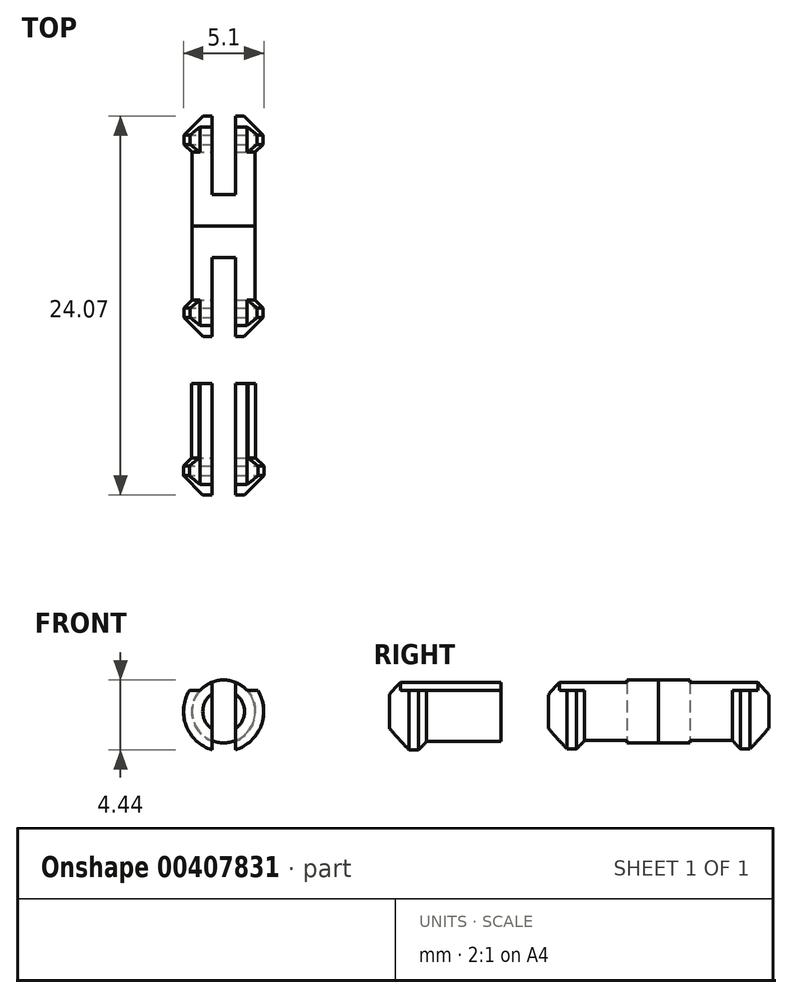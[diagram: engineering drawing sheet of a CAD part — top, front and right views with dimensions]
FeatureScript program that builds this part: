
annotation { "Feature Type Name" : "Feature", "Feature Type Description" : "" }
export const myFeature = defineFeature(function(context is Context, id is Id, definition is map)
    precondition{}
    {
        {
            var Q0;
            Q0=qCreatedBy(makeId("Front.planeOp"),FACE);
            var sketch = newSketch(context, id + "F0", { "sketchPlane" : qUnion([Q0])});
            skCircle(sketch, "E0", {"center": v(0, 0) * mm, "radius": 2 * mm});
            skLineSegment(sketch, "E1", {"start": v(-2, 0) * mm, "end": v(2, 0) * mm, "construction": true});
            skSolve(sketch);
        }
        {
            var Q0;
            Q0=makeQuery(id+"F0.imprint","IMPRINT",FACE,{"disambiguationData":[TD([[makeQuery(id+"F0.imprint","IMPRINT",EDGE,{"derivedFrom":sQuery(id+"F0.wireOp",EDGE,"E0")}),1.0]])]});
            extrude(context, id + "F1", {"entities" : qUnion([Q0]), "depth" : 4 * mm});
        }
        {
            var Q0;
            Q0=makeQuery(id+"F1.opExtrude","CAP_FACE",FACE,{"disambiguationData":[OSD([sQuery(id+"F0.wireOp",EDGE,"E0")])],"isStart":false});
            var sketch = newSketch(context, id + "F2", { "sketchPlane" : qUnion([Q0])});
            skCircle(sketch, "E2.0", {"center": v(0, 0) * mm, "radius": 2.5 * mm});
            skSolve(sketch);
        }
        {
            var Q0;
            Q0=makeQuery(id+"F2.imprint","IMPRINT",FACE,{"disambiguationData":[TD([[makeQuery(id+"F2.imprint","IMPRINT",EDGE,{"derivedFrom":makeQuery(id+"F1.opExtrude","CAP_EDGE",EDGE,{"disambiguationData":[OSD([sQuery(id+"F0.wireOp",EDGE,"E0")])],"isStart":false})}),1.0]])]});
            var Q1;
            Q1=makeQuery(id+"F2.imprint","IMPRINT",FACE,{"disambiguationData":[TD([[makeQuery(id+"F2.imprint","IMPRINT",EDGE,{"derivedFrom":sQuery(id+"F2.wireOp",EDGE,"E2.0")}),1.0]])]});
            var Q2;
            Q2=sQuery(id+"F2.wireOp",EDGE,"E2.0");
            extrude(context, id + "F3", {"entities" : qUnion([Q0, Q1]), "operationType" : NewBodyOperationType.ADD, "surfaceEntities" : qUnion([Q2]), "depth" : 3 * mm});
        }
        {
            var Q0;
            Q0=makeQuery(id+"F3.opExtrude","CAP_EDGE",EDGE,{"disambiguationData":[OSD([sQuery(id+"F2.wireOp",EDGE,"E2.0")])],"isStart":false});
            var Q1;
            Q1=makeQuery(id+"F3.opExtrude","CAP_EDGE",EDGE,{"disambiguationData":[OSD([sQuery(id+"F2.wireOp",EDGE,"E2.0")])],"isStart":true});
            chamfer(context, id + "F4", {"entities" : qUnion([Q0, Q1]), "chamferType" : ChamferType.OFFSET_ANGLE, "width" : 1.2 * mm, "oppositeDirection" : false, "angle" : 45 * degree, "tangentPropagation" : true});
        }
        {
            var Q0;
            Q0=qCreatedBy(makeId("Right.planeOp"),FACE);
            var sketch = newSketch(context, id + "F5", { "sketchPlane" : qUnion([Q0])});
            skLineSegment(sketch, "E3.0", {"start": v(-7, -1.3) * mm, "end": v(-7, 1.3) * mm, "construction": true});
            skLineSegment(sketch, "E4.0", {"start": v(0, -2) * mm, "end": v(0, 2) * mm, "construction": true});
            skLineSegment(sketch, "E5", {"start": v(0, 0) * mm, "end": v(-7, 0) * mm, "construction": true});
            skPoint(sketch, "E6", {"position": v(-3.5, 0) * mm});
            skSolve(sketch);
        }
        {
            var Q0;
            Q0=makeQuery(id+"F1.opExtrude","SWEPT_BODY",BODY,{"disambiguationData":[OSD([sQuery(id+"F0.wireOp",EDGE,"E0")])]});
            var Q1;
            Q1=sQuery(id+"F5.wireOp",VERTEX,"E6");
            transform(context, id + "F6", {"entities" : qUnion([Q0]), "transformType" : TransformType.SCALE_UNIFORMLY, "scale" : 1.02, "scalePoint" : qUnion([Q1]), "makeCopy" : true});
        }
        {
            var Q0;
            Q0=makeQuery(id+"F6.opPattern","COPY",FACE,{"derivedFrom":makeQuery(id+"F1.opExtrude","CAP_FACE",FACE,{"disambiguationData":[OSD([sQuery(id+"F0.wireOp",EDGE,"E0")])],"isStart":true}),"instanceName":"1"});
            var Q1;
            Q1=makeQuery(id+"F1.opExtrude","CAP_FACE",FACE,{"disambiguationData":[OSD([sQuery(id+"F0.wireOp",EDGE,"E0")])],"isStart":true});
            extrude(context, id + "F7", {"entities" : qUnion([Q0]), "operationType" : NewBodyOperationType.REMOVE, "endBound" : BoundingType.UP_TO_SURFACE, "oppositeDirection" : true, "endBoundEntityFace" : qUnion([Q1]), "depth" : 25 * mm});
        }
        {
            var Q0;
            Q0=makeQuery(id+"F6.opPattern","COPY",BODY,{"derivedFrom":makeQuery(id+"F1.opExtrude","SWEPT_BODY",BODY,{"disambiguationData":[OSD([sQuery(id+"F0.wireOp",EDGE,"E0")])]}),"instanceName":"1"});
            var Q1;
            Q1=sQuery(id+"F5.wireOp",EDGE,"E5");
            transform(context, id + "F8", {"entities" : qUnion([Q0]), "transformType" : TransformType.TRANSLATION_DISTANCE, "transformDirection" : qUnion([Q1]), "distance" : 10 * mm, "makeCopy" : false});
        }
        {
            var Q0;
            Q0=qCreatedBy(makeId("Right.planeOp"),FACE);
            var sketch = newSketch(context, id + "F9", { "sketchPlane" : qUnion([Q0])});
            skPoint(sketch, "E7.0", {"position": v(0, 0) * mm});
            skLineSegment(sketch, "E8", {"start": v(0, 0) * mm, "end": v(-2, 0) * mm, "construction": true});
            skSolve(sketch);
        }
        {
            var Q0;
            Q0=makeQuery(id+"F0.imprint","IMPRINT",FACE,{"disambiguationData":[TD([[makeQuery(id+"F0.imprint","IMPRINT",EDGE,{"derivedFrom":sQuery(id+"F0.wireOp",EDGE,"E0")}),1.0]])]});
            var Q1;
            Q1=sQuery(id+"F9.wireOp",VERTEX,"E8.end");
            cPlane(context, id + "F10", {"entities" : qUnion([Q0, Q1]), "cplaneType" : CPlaneType.PLANE_POINT, "offset" : 25 * mm, "width" : 150 * mm, "height" : 150 * mm});
        }
        {
            var Q0;
            Q0=qCreatedBy(id+"F10.planeOp",FACE);
            var sketch = newSketch(context, id + "F11", { "sketchPlane" : qUnion([Q0])});
            skCircle(sketch, "E9.0", {"center": v(0, 0) * mm, "radius": 2 * mm, "construction": true});
            skLineSegment(sketch, "E10", {"start": v(-0.75, 1.85) * mm, "end": v(0.75, 1.85) * mm, "construction": true});
            skLineSegment(sketch, "E11.bottom", {"start": v(0.75, 5.02) * mm, "end": v(-0.75, 5.02) * mm});
            skLineSegment(sketch, "E11.top", {"start": v(0.75, -5.02) * mm, "end": v(-0.75, -5.02) * mm});
            skLineSegment(sketch, "E11.left", {"start": v(0.75, 5.02) * mm, "end": v(0.75, -5.02) * mm});
            skLineSegment(sketch, "E11.right", {"start": v(-0.75, 5.02) * mm, "end": v(-0.75, -5.02) * mm});
            skSolve(sketch);
        }
        {
            var Q0;
            Q0=makeQuery(id+"F11.imprint","IMPRINT",FACE,{"disambiguationData":[TD([[makeQuery(id+"F11.imprint","IMPRINT",EDGE,{"derivedFrom":sQuery(id+"F11.wireOp",EDGE,"E11.bottom")}),1.0]])]});
            extrude(context, id + "F12", {"entities" : qUnion([Q0]), "operationType" : NewBodyOperationType.REMOVE, "depth" : 25 * mm});
        }
        {
            var Q0;
            Q0=makeQuery(id+"F1.opExtrude","CAP_FACE",FACE,{"disambiguationData":[OSD([sQuery(id+"F0.wireOp",EDGE,"E0")])],"isStart":true});
            var sketch = newSketch(context, id + "F13", { "sketchPlane" : qUnion([Q0])});
            skCircle(sketch, "E12.0", {"center": v(0, 0) * mm, "radius": 2 * mm, "construction": true});
            skLineSegment(sketch, "E13", {"start": v(-1.5, 1.32) * mm, "end": v(1.5, 1.32) * mm});
            skLineSegment(sketch, "E14.bottom", {"start": v(-4.18, 1.32) * mm, "end": v(4.7, 1.32) * mm});
            skLineSegment(sketch, "E14.top", {"start": v(-4.18, 3.46) * mm, "end": v(4.7, 3.46) * mm});
            skLineSegment(sketch, "E14.left", {"start": v(-4.18, 1.32) * mm, "end": v(-4.18, 3.46) * mm});
            skLineSegment(sketch, "E14.right", {"start": v(4.7, 1.32) * mm, "end": v(4.7, 3.46) * mm});
            skSolve(sketch);
        }
        {
            var Q0;
            Q0=makeQuery(id+"F13.imprint","IMPRINT",FACE,{"disambiguationData":[TD([[makeQuery(id+"F13.imprint","IMPRINT",EDGE,{"derivedFrom":sQuery(id+"F13.wireOp",EDGE,"E14.top")}),-1.0]])]});
            var Q1;
            {var subQ0=sQuery(id+"F13.wireOp",EDGE,"E14.bottom");var subQ1=makeQuery(id+"F1.opExtrude","CAP_EDGE",EDGE,{"disambiguationData":[OSD([sQuery(id+"F0.wireOp",EDGE,"E0")])],"isStart":true});var subQ2=makeQuery(id+"F13.imprint","INTERSECT",VERTEX,{"disambiguationData":[OD(0.0)],"derivedFrom":[subQ1,subQ0]});Q1=makeQuery(id+"F13.imprint","IMPRINT",FACE,{"disambiguationData":[TD([[makeQuery(id+"F13.imprint","IMPRINT",EDGE,{"disambiguationData":[TD([[subQ2,-1.0]])],"derivedFrom":subQ0}),1.0]])]});}
            extrude(context, id + "F14", {"entities" : qUnion([Q0, Q1]), "operationType" : NewBodyOperationType.REMOVE, "endBound" : BoundingType.THROUGH_ALL, "oppositeDirection" : true, "depth" : 25 * mm});
        }
        {
            var Q0;
            Q0=makeQuery(id+"F1.opExtrude","SWEPT_BODY",BODY,{"disambiguationData":[OSD([sQuery(id+"F0.wireOp",EDGE,"E0")])]});
            var Q1;
            Q1=qCreatedBy(makeId("Front.planeOp"),FACE);
            mirror(context, id + "F15", {"operationType" : NewBodyOperationType.ADD, "entities" : qUnion([Q0]), "mirrorPlane" : qUnion([Q1])});
        }
    });
